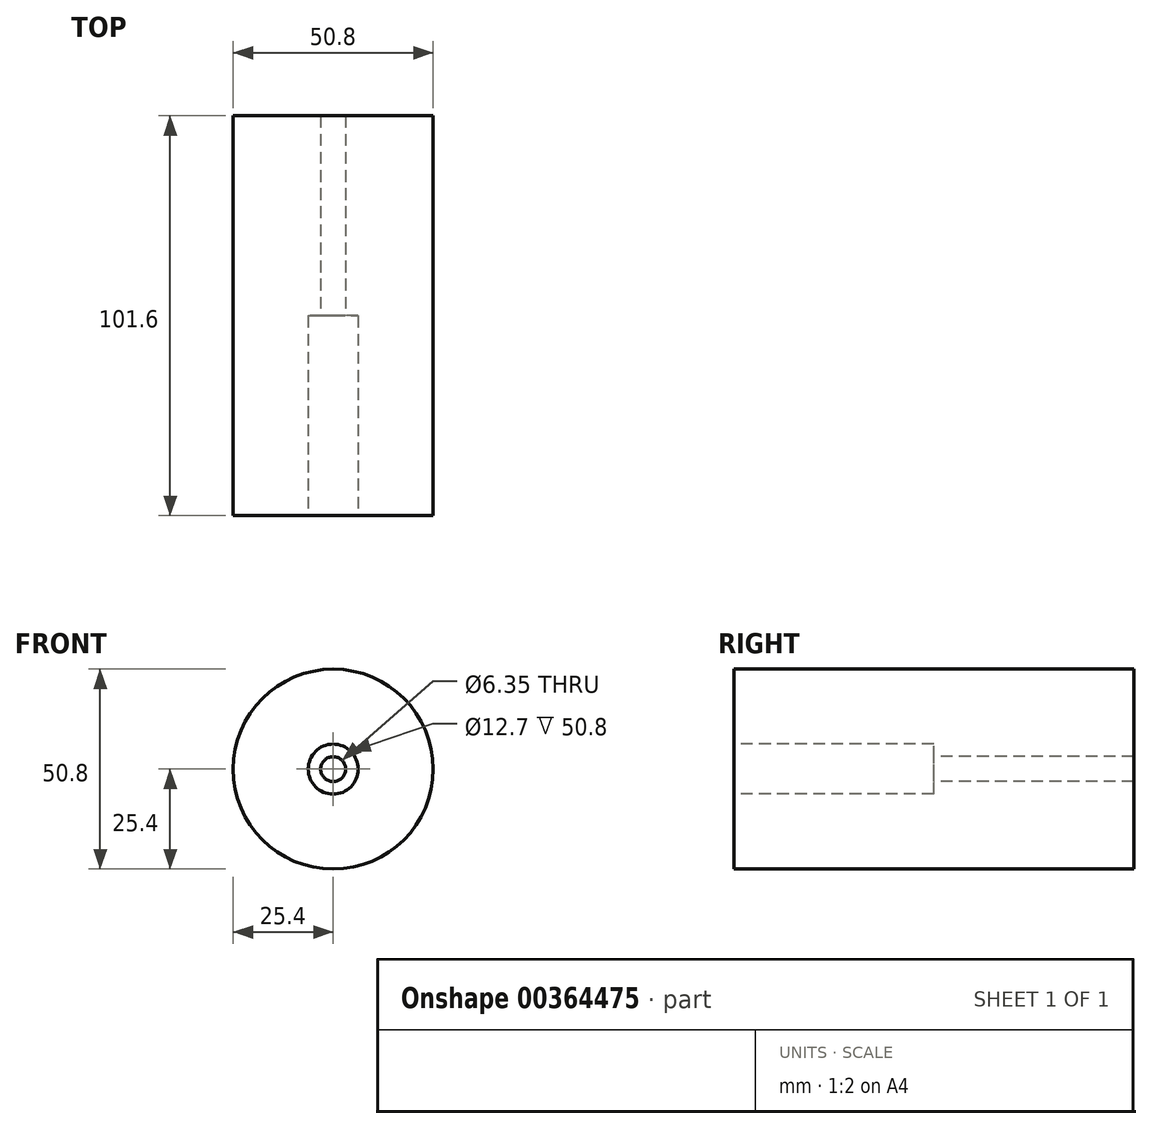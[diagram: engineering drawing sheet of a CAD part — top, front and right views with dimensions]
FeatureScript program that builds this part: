
annotation { "Feature Type Name" : "Feature", "Feature Type Description" : "" }
export const myFeature = defineFeature(function(context is Context, id is Id, definition is map)
    precondition{}
    {
        {
            var Q0;
            Q0=qCreatedBy(makeId("Front.planeOp"),FACE);
            var sketch = newSketch(context, id + "F0", { "sketchPlane" : qUnion([Q0])});
            skCircle(sketch, "E0", {"center": v(0, 0) * mm, "radius": 25.4 * mm});
            skSolve(sketch);
        }
        {
            var Q0;
            Q0 = qSketchRegion(id + "F0", true);
            var Q1;
            Q1=makeQuery(id+"F0.imprint","IMPRINT",FACE,{"disambiguationData":[TD([[makeQuery(id+"F0.imprint","IMPRINT",EDGE,{"derivedFrom":sQuery(id+"F0.wireOp",EDGE,"E0")}),1.0]])]});
            extrude(context, id + "F1", {"entities" : qUnion([Q0, Q1]), "depth" : 101.6 * mm});
        }
        {
            var Q0;
            Q0=makeQuery(id+"F1.opExtrude","CAP_FACE",FACE,{"disambiguationData":[OSD([sQuery(id+"F0.wireOp",EDGE,"E0")])],"isStart":false});
            var sketch = newSketch(context, id + "F2", { "sketchPlane" : qUnion([Q0])});
            skCircle(sketch, "E1", {"center": v(0, 0) * mm, "radius": 6.35 * mm});
            skSolve(sketch);
        }
        {
            var Q0;
            Q0=sQuery(id+"F2.wireOp",VERTEX,"E1.center");
            var Q1;
            Q1=makeQuery(id+"F1.opExtrude","SWEPT_BODY",BODY,{"disambiguationData":[OSD([sQuery(id+"F0.wireOp",EDGE,"E0")])]});
            hole(context, id + "F3", {"style" : HoleStyle.C_BORE, "endStyle" : HoleEndStyle.THROUGH, "holeDiameter" : 6.35 * mm, "cBoreDiameter" : 12.7 * mm, "cBoreDepth" : 50.8 * mm, "isTappedThrough" : true, "tappedDepth" : 12.7 * mm, "tapClearance" : 3, "startFromSketch" : true, "locations" : qUnion([Q0]), "scope" : qUnion([Q1])});
        }
    });
